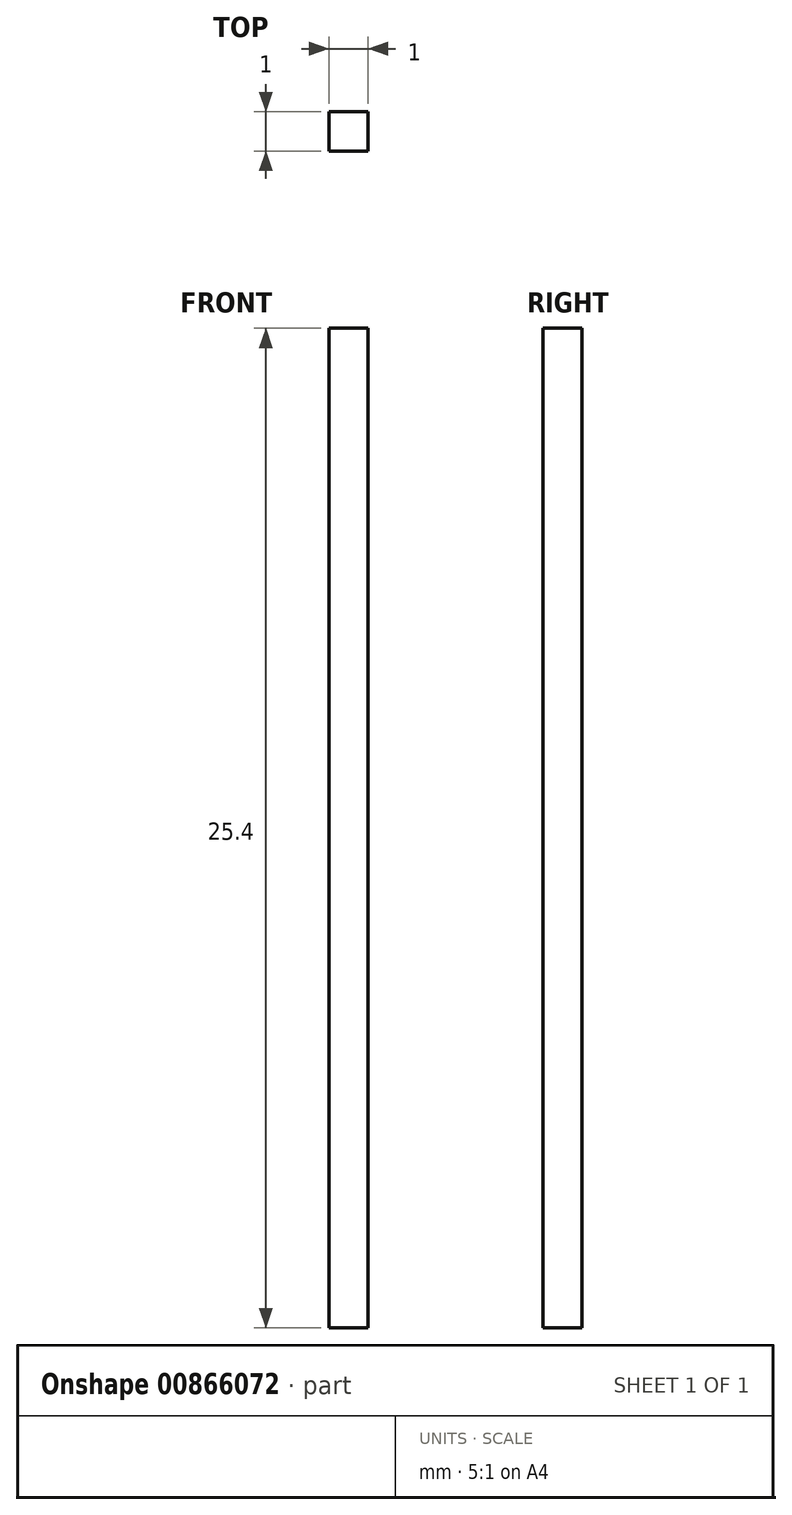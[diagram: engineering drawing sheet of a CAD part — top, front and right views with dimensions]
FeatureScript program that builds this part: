
annotation { "Feature Type Name" : "Feature", "Feature Type Description" : "" }
export const myFeature = defineFeature(function(context is Context, id is Id, definition is map)
    precondition{}
    {
        {
            var Q0;
            Q0=qCreatedBy(makeId("Top.planeOp"),FACE);
            var sketch = newSketch(context, id + "F0", { "sketchPlane" : qUnion([Q0])});
            skLineSegment(sketch, "E0.bottom", {"start": v(0, 0) * mm, "end": v(1, 0) * mm});
            skLineSegment(sketch, "E0.top", {"start": v(0, 1) * mm, "end": v(1, 1) * mm});
            skLineSegment(sketch, "E0.left", {"start": v(0, 0) * mm, "end": v(0, 1) * mm});
            skLineSegment(sketch, "E0.right", {"start": v(1, 0) * mm, "end": v(1, 1) * mm});
            skSolve(sketch);
        }
        {
            var Q0;
            Q0=makeQuery(id+"F0.imprint","IMPRINT",FACE,{"disambiguationData":[TD([[makeQuery(id+"F0.imprint","IMPRINT",EDGE,{"derivedFrom":sQuery(id+"F0.wireOp",EDGE,"E0.bottom")}),1.0]])]});
            extrude(context, id + "F1", {"entities" : qUnion([Q0]), "depth" : 25.4 * mm, "offsetDistance" : 25.4 * mm});
        }
    });
